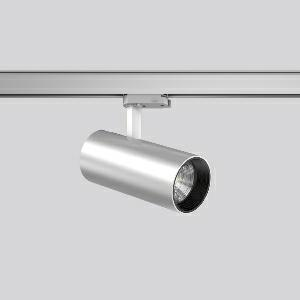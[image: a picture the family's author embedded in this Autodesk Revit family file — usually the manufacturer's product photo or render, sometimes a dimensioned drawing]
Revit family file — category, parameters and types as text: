
# Revit family: deecos_s_mini_742194_004_cc9c
name_source: partatom
category: Lighting Fixtures
units: mm (PartAtom-declared; Revit-internal decimal feet)

## family parameters
Cut with Voids When Loaded = No
Host = Face
Light Source = No
Part Type = Normal
Room Calculation Point = No
Round Connector Dimension = Use Diameter
Shared = No

## types (1)
- DEECOS S mini (1 x LED Modul 930, 2000 lm, 3000)
    Apparent Load = 22 VA
    Approval mark = CE
    CIE Flux Codes = 99 100 100 100 100
    Color Rendering = 90
    Color Temperature = 3000
    Default Elevation = 1800 mm
    Description = Series: DEECOS S mini
LED surface-mounted projector in modern design with no visible cooling ribs. Housing: die-cast aluminium, powder-coated. Rotation range: 356°. Swivel range: 90°. Black plastic ring and recessed LED to prevent glare from the side. Optical assembly with lens made of plastic (polycarbonate) for the best homogeneous light distribution - can be changed without tools. Best colour rendering index Ra>90. Superspot version with small spot LED. With multi adaptor for 3-circuit tracks 230 V. Suitable for Track on ceiling, Wall track. High quality converter without flickering and stroboscopic effect. The following accessories can be mounted without use of tools: interchangeable lenses, decorative glasses, honeycomb louvre, clear and frosted diffusers, white interchangeable plastic ring. 
Colour: silver
Diameter: 87 mm
Height: 214 mm
Lamp: LED
Socket: without socket
Colour temperature: 3000K
Colour rendering index (CRI): 92
System power: 22 W
Rated luminous flux: 2000 lm
Luminous efficiency: 91 lm/W
Control gear: Regulated power supply
Protection class: I
Type of protection: IP 20
    Height = 214 mm
    Lamp = 1 x LED Modul 930
    Lamp Light Flux = 2000 lm
    Lamp count = 1
    Length = 87 mm
    Lifetime = 50000 h
    Luminous efficacy = 91 lm/W
    Manufacturer = RZB
    ModVariant = No
    Model = 742194.004
    Mounting Place = Ceiling
    Mounting Type = Rail mounted
    Number of Poles = 1
    OnlyDefault = Yes
    Power Factor = 1
    Product Name = DEECOS S mini
    Product group = Track mounted projectors
    ProductGroupID = 301
    Protection Class = Protection class I
    Protection Degree = IP 20
    RLX_Detail_Level = 1
    RLX_Emergency_Light_Flux = 0 lm
    RLX_Emergency_Type = 0
    RLX_Emergency_Type_DB = No
    RlxData = <blob elided: 37037 chars, md5=d5bf1e7b>
    Socket = socket
    Standby Power = 0 W
    System Light Flux = 2000 lm
    System Power = 22 W
    Type Comments = Product without accessories
    Type Image = 741930.004.jpg
    URL = http://relux.com
    VarID = ---
    Voltage = 230 V
    Voltage Range = 220-240 V
    Weight = 0.00 kg
    Width = 0 mm  [stored 0 ft]

note: [stored X ft] marks values corroborated as IEEE doubles in the binary element streams (Revit-internal decimal feet)

## geometry (parser evidence)
native form markers: Blend x4, Sweep x12
no freeform markers — native parametric forms only
